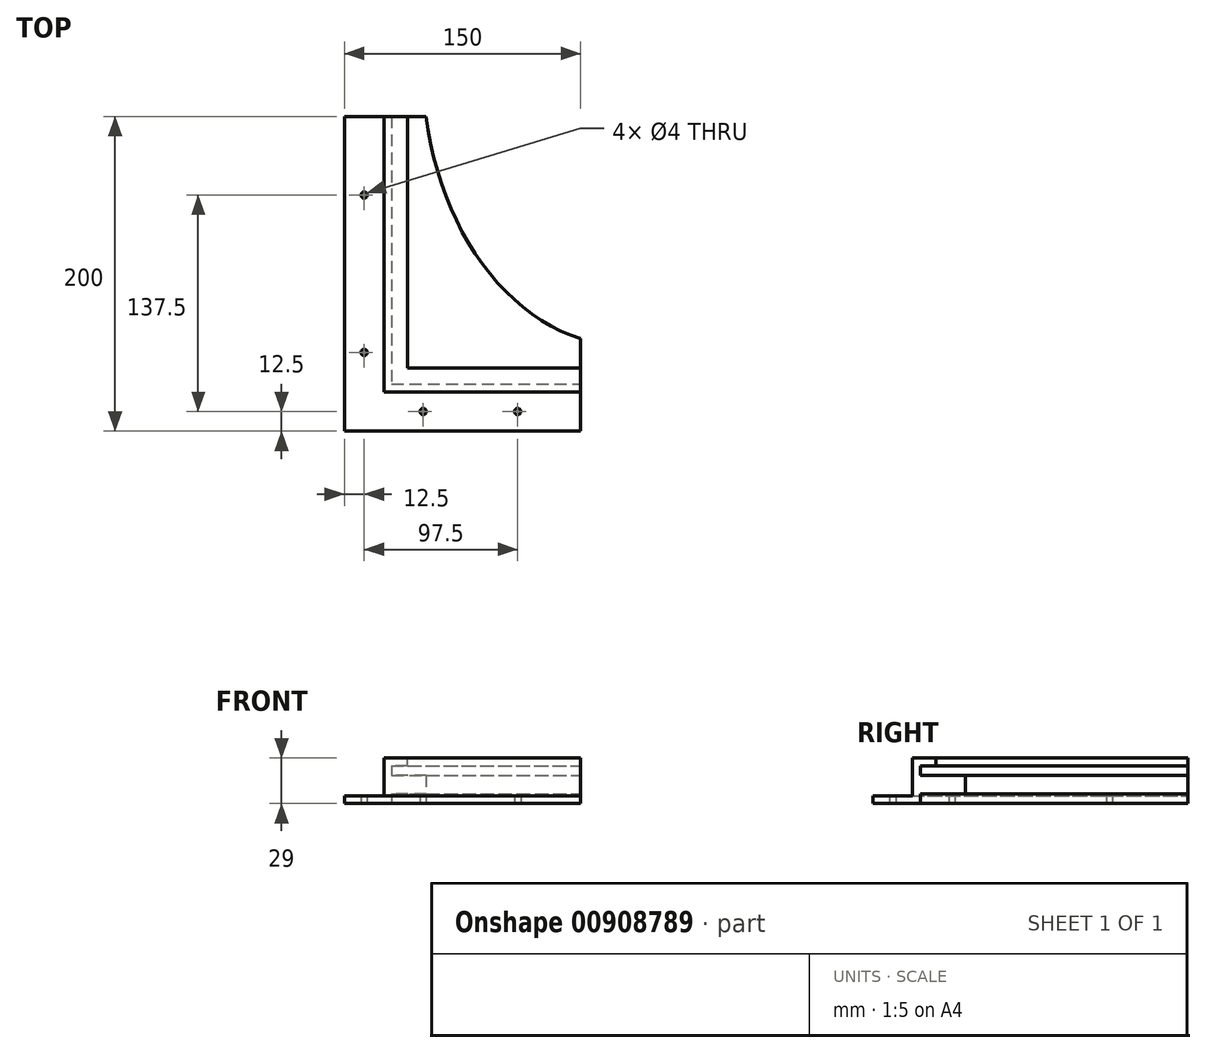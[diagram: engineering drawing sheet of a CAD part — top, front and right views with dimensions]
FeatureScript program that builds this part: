
annotation { "Feature Type Name" : "Feature", "Feature Type Description" : "" }
export const myFeature = defineFeature(function(context is Context, id is Id, definition is map)
    precondition{}
    {
        {
            var Q0;
            Q0=qCreatedBy(makeId("Top.planeOp"),FACE);
            var sketch = newSketch(context, id + "F0", { "sketchPlane" : qUnion([Q0])});
            skEllipticalArc(sketch, "E0", {});
            skLineSegment(sketch, "E1", {"start": v(-130, 0) * mm, "end": v(-130, -176) * mm});
            skPoint(sketch, "E1.endSnap0", {"position": v(0, -176) * mm});
            skLineSegment(sketch, "E2", {"start": v(-130, -176) * mm, "end": v(0, -176) * mm});
            skLineSegment(sketch, "E3", {"start": v(-130, 0) * mm, "end": v(-150, 0) * mm});
            skLineSegment(sketch, "E4", {"start": v(-150, 0) * mm, "end": v(-150, -200) * mm});
            skLineSegment(sketch, "E5", {"start": v(-150, -200) * mm, "end": v(0, -200) * mm});
            skLineSegment(sketch, "E6", {"start": v(0, -200) * mm, "end": v(0, -176) * mm});
            const initialGuessF0  = {"E0": [0, 0, 1, 0, 0.13, 0.176, 3.141592653589793, 4.71238898038469]};
            skSetInitialGuess(sketch, initialGuessF0);
            skSolve(sketch);
        }
        {
            var Q0;
            Q0=qSketchRegion(id+"F0",true);
            extrude(context, id + "F1", {"entities" : qUnion([Q0]), "depth" : 12 * mm, "offsetDistance" : 25 * mm});
        }
        {
            var Q0;
            Q0=makeQuery(id+"F1.opExtrude","SWEPT_FACE",FACE,{"disambiguationData":[OSD([sQuery(id+"F0.wireOp",EDGE,"E5")])]});
            var sketch = newSketch(context, id + "F2", { "sketchPlane" : qUnion([Q0])});
            skLineSegment(sketch, "E7.bottom", {"start": v(-150, 18) * mm, "end": v(0, 18) * mm});
            skLineSegment(sketch, "E7.top", {"start": v(-150, -6) * mm, "end": v(0, -6) * mm});
            skLineSegment(sketch, "E7.left", {"start": v(-150, 18) * mm, "end": v(-150, -6) * mm});
            skLineSegment(sketch, "E7.right", {"start": v(0, 18) * mm, "end": v(0, -6) * mm});
            skSolve(sketch);
        }
        {
            var Q0;
            Q0=qSketchRegion(id+"F2",true);
            extrude(context, id + "F3", {"entities" : qUnion([Q0]), "operationType" : NewBodyOperationType.ADD, "depth" : 5 * mm, "offsetDistance" : 25 * mm});
        }
        {
            var Q0;
            Q0=makeQuery(id+"F3.boolean.opBoolean","MERGE",FACE,{"derivedFrom":[makeQuery(id+"F1.opExtrude","SWEPT_FACE",FACE,{"disambiguationData":[OSD([sQuery(id+"F0.wireOp",EDGE,"E4")])]}),makeQuery(id+"F3.opExtrude","SWEPT_FACE",FACE,{"disambiguationData":[OSD([sQuery(id+"F2.wireOp",EDGE,"E7.left")])]})]});
            var sketch = newSketch(context, id + "F4", { "sketchPlane" : qUnion([Q0])});
            skLineSegment(sketch, "E8.bottom", {"start": v(205, 18) * mm, "end": v(0, 18) * mm});
            skLineSegment(sketch, "E8.top", {"start": v(205, -6) * mm, "end": v(0, -6) * mm});
            skLineSegment(sketch, "E8.left", {"start": v(205, 18) * mm, "end": v(205, -6) * mm});
            skLineSegment(sketch, "E8.right", {"start": v(0, 18) * mm, "end": v(0, -6) * mm});
            skSolve(sketch);
        }
        {
            var Q0;
            Q0=qSketchRegion(id+"F4",true);
            extrude(context, id + "F5", {"entities" : qUnion([Q0]), "operationType" : NewBodyOperationType.ADD, "depth" : 5 * mm, "offsetDistance" : 25 * mm});
        }
        {
            var Q0;
            Q0=makeQuery(id+"F5.boolean.opBoolean","MERGE",FACE,{"derivedFrom":[makeQuery(id+"F3.opExtrude","SWEPT_FACE",FACE,{"disambiguationData":[OSD([sQuery(id+"F2.wireOp",EDGE,"E7.top")])]}),makeQuery(id+"F5.opExtrude","SWEPT_FACE",FACE,{"disambiguationData":[OSD([sQuery(id+"F4.wireOp",EDGE,"E8.top")])]})]});
            var sketch = newSketch(context, id + "F6", { "sketchPlane" : qUnion([Q0])});
            skLineSegment(sketch, "E9", {"start": v(0, 230) * mm, "end": v(-180, 230) * mm});
            skLineSegment(sketch, "E10", {"start": v(-180, 230) * mm, "end": v(-180, 0) * mm});
            skLineSegment(sketch, "E11", {"start": v(-180, 0) * mm, "end": v(-155, 0) * mm});
            skLineSegment(sketch, "E12", {"start": v(-155, 0) * mm, "end": v(-155, 205) * mm});
            skLineSegment(sketch, "E13", {"start": v(-155, 205) * mm, "end": v(0, 205) * mm});
            skLineSegment(sketch, "E14", {"start": v(0, 205) * mm, "end": v(0, 230) * mm});
            skCircle(sketch, "E15", {"center": v(-167.5, 80) * mm, "radius": 2 * mm});
            skCircle(sketch, "E16", {"center": v(-167.5, 180) * mm, "radius": 2 * mm});
            skCircle(sketch, "E17", {"center": v(-130, 217.5) * mm, "radius": 2 * mm});
            skCircle(sketch, "E18", {"center": v(-70, 217.5) * mm, "radius": 2 * mm});
            skSolve(sketch);
        }
        {
            var Q0;
            Q0=qSketchRegion(id+"F6",true);
            extrude(context, id + "F7", {"entities" : qUnion([Q0]), "operationType" : NewBodyOperationType.ADD, "oppositeDirection" : true, "depth" : 5 * mm, "offsetDistance" : 25 * mm});
        }
        {
            var Q0;
            Q0=makeQuery(id+"F5.boolean.opBoolean","MERGE",FACE,{"derivedFrom":[makeQuery(id+"F3.opExtrude","SWEPT_FACE",FACE,{"disambiguationData":[OSD([sQuery(id+"F2.wireOp",EDGE,"E7.bottom")])]}),makeQuery(id+"F5.opExtrude","SWEPT_FACE",FACE,{"disambiguationData":[OSD([sQuery(id+"F4.wireOp",EDGE,"E8.bottom")])]})]});
            var sketch = newSketch(context, id + "F8", { "sketchPlane" : qUnion([Q0])});
            skLineSegment(sketch, "E19", {"start": v(-155, 0) * mm, "end": v(-140, 0) * mm});
            skLineSegment(sketch, "E20", {"start": v(-140, 0) * mm, "end": v(-140, -190) * mm});
            skLineSegment(sketch, "E21", {"start": v(-140, -190) * mm, "end": v(0, -190) * mm});
            skLineSegment(sketch, "E22", {"start": v(0, -190) * mm, "end": v(0, -205) * mm});
            skLineSegment(sketch, "E23", {"start": v(0, -205) * mm, "end": v(-155, -205) * mm});
            skLineSegment(sketch, "E24", {"start": v(-155, -205) * mm, "end": v(-155, 0) * mm});
            skSolve(sketch);
        }
        {
            var Q0;
            Q0=qSketchRegion(id+"F8",true);
            extrude(context, id + "F9", {"entities" : qUnion([Q0]), "operationType" : NewBodyOperationType.ADD, "depth" : 5 * mm, "offsetDistance" : 25 * mm});
        }
        {
            var Q0;
            Q0=qCreatedBy(makeId("Top.planeOp"),FACE);
            var sketch = newSketch(context, id + "F10", { "sketchPlane" : qUnion([Q0])});
            skLineSegment(sketch, "E25.bottom", {"start": v(0, 0) * mm, "end": v(-180, 0) * mm});
            skLineSegment(sketch, "E25.top", {"start": v(0, -30) * mm, "end": v(-180, -30) * mm});
            skLineSegment(sketch, "E25.left", {"start": v(0, 0) * mm, "end": v(0, -30) * mm});
            skLineSegment(sketch, "E25.right", {"start": v(-180, 0) * mm, "end": v(-180, -30) * mm});
            skLineSegment(sketch, "E26.bottom", {"start": v(0, 0) * mm, "end": v(-30, 0) * mm});
            skLineSegment(sketch, "E26.top", {"start": v(0, -230) * mm, "end": v(-30, -230) * mm});
            skLineSegment(sketch, "E26.left", {"start": v(0, 0) * mm, "end": v(0, -230) * mm});
            skLineSegment(sketch, "E26.right", {"start": v(-30, 0) * mm, "end": v(-30, -230) * mm});
            skSolve(sketch);
        }
        {
            var Q0;
            Q0 = qSketchRegion(id + "F10", true);
            extrude(context, id + "F11", {"entities" : qUnion([Q0]), "operationType" : NewBodyOperationType.REMOVE, "endBound" : BoundingType.SYMMETRIC, "oppositeDirection" : true, "depth" : 50 * mm, "offsetDistance" : 25 * mm});
        }
    });
